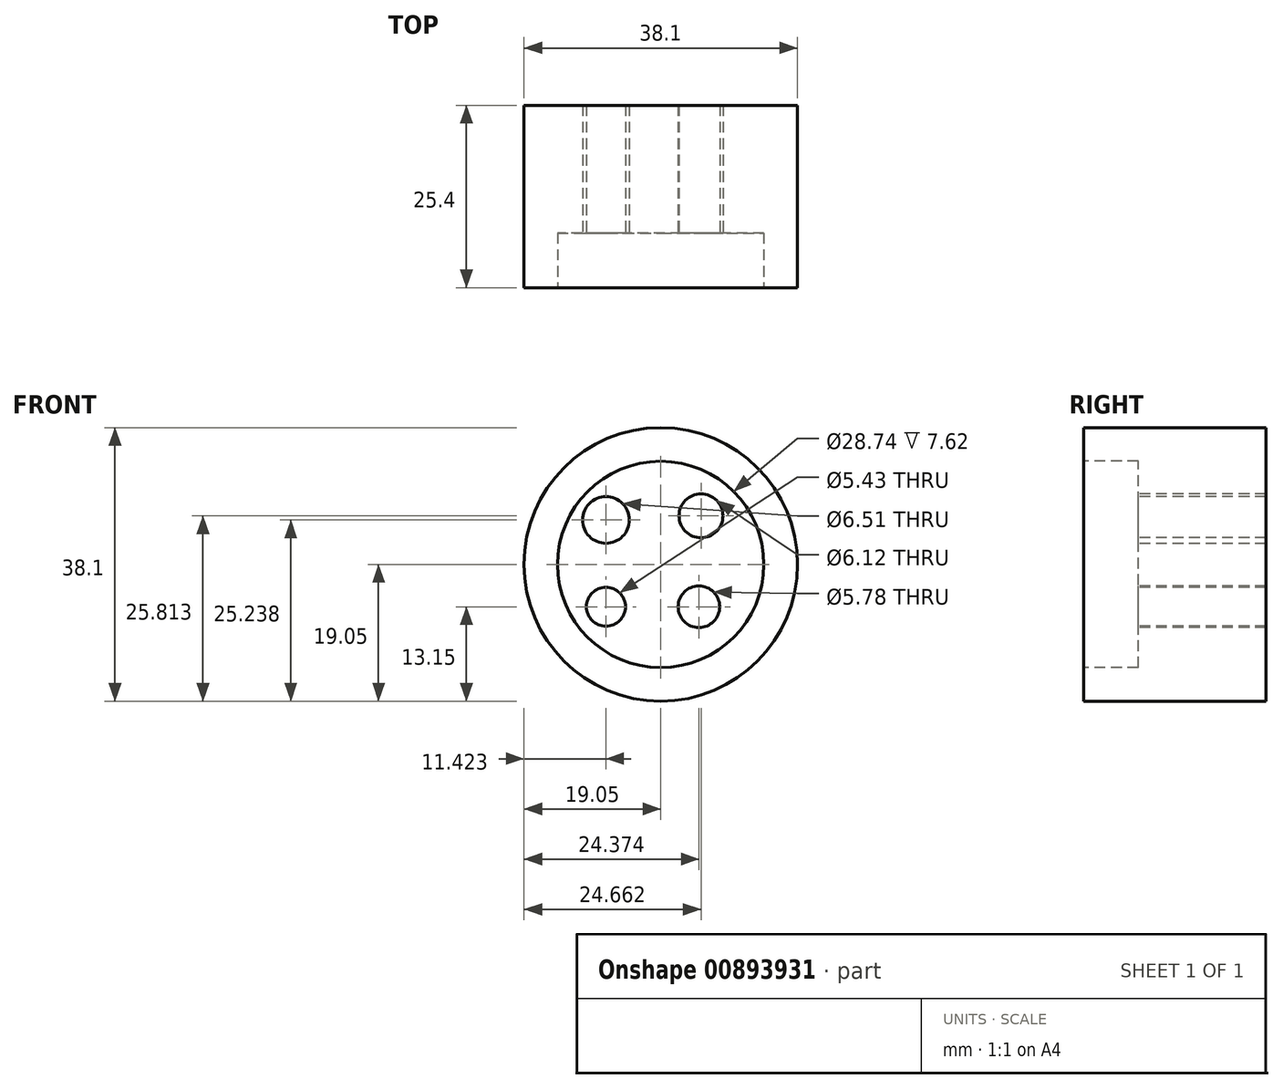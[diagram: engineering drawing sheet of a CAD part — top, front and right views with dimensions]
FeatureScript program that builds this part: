
annotation { "Feature Type Name" : "Feature", "Feature Type Description" : "" }
export const myFeature = defineFeature(function(context is Context, id is Id, definition is map)
    precondition{}
    {
        {
            var Q0;
            Q0=qCreatedBy(makeId("Front.planeOp"),FACE);
            var sketch = newSketch(context, id + "F0", { "sketchPlane" : qUnion([Q0])});
            skCircle(sketch, "E0", {"center": v(0, 0) * mm, "radius": 19.05 * mm});
            skCircle(sketch, "E1", {"center": v(0, 0) * mm, "radius": 14.35 * mm});
            skSolve(sketch);
        }
        {
            var Q0;
            Q0 = qSketchRegion(id + "F0", true);
            var Q1;
            Q1=makeQuery(id+"F0.imprint","IMPRINT",FACE,{"disambiguationData":[TD([[makeQuery(id+"F0.imprint","IMPRINT",EDGE,{"derivedFrom":sQuery(id+"F0.wireOp",EDGE,"E1")}),1.0]])]});
            extrude(context, id + "F1", {"entities" : qUnion([Q0, Q1]), "depth" : 25.4 * mm, "offsetDistance" : 25.4 * mm});
        }
        {
            var Q0;
            Q0=makeQuery(id+"F1.opExtrude","CAP_FACE",FACE,{"disambiguationData":[OSD([sQuery(id+"F0.wireOp",EDGE,"E0")])],"isStart":false});
            var sketch = newSketch(context, id + "F2", { "sketchPlane" : qUnion([Q0])});
            skCircle(sketch, "E2", {"center": v(0, 0) * mm, "radius": 14.37 * mm});
            skSolve(sketch);
        }
        {
            var Q0;
            Q0 = qSketchRegion(id + "F2", true);
            extrude(context, id + "F3", {"entities" : qUnion([Q0]), "operationType" : NewBodyOperationType.REMOVE, "oppositeDirection" : true, "depth" : 7.62 * mm, "offsetDistance" : 25.4 * mm});
        }
        {
            var Q0;
            Q0=makeQuery(id+"F3.boolean.opBoolean","COPY",FACE,{"derivedFrom":makeQuery(id+"F3.opExtrude","CAP_FACE",FACE,{"disambiguationData":[OSD([sQuery(id+"F2.wireOp",EDGE,"E2")])],"isStart":false})});
            var sketch = newSketch(context, id + "F4", { "sketchPlane" : qUnion([Q0])});
            skCircle(sketch, "E3", {"center": v(-7.63, -5.9) * mm, "radius": 2.72 * mm});
            skCircle(sketch, "E4", {"center": v(-7.63, 6.19) * mm, "radius": 3.26 * mm});
            skCircle(sketch, "E5", {"center": v(5.61, 6.76) * mm, "radius": 3.06 * mm});
            skCircle(sketch, "E6", {"center": v(5.32, -5.9) * mm, "radius": 2.9 * mm});
            skSolve(sketch);
        }
        {
            var Q0;
            Q0 = qSketchRegion(id + "F4", true);
            extrude(context, id + "F5", {"entities" : qUnion([Q0]), "operationType" : NewBodyOperationType.REMOVE, "endBound" : BoundingType.THROUGH_ALL, "oppositeDirection" : true, "depth" : 25.4 * mm, "offsetDistance" : 25.4 * mm});
        }
    });
